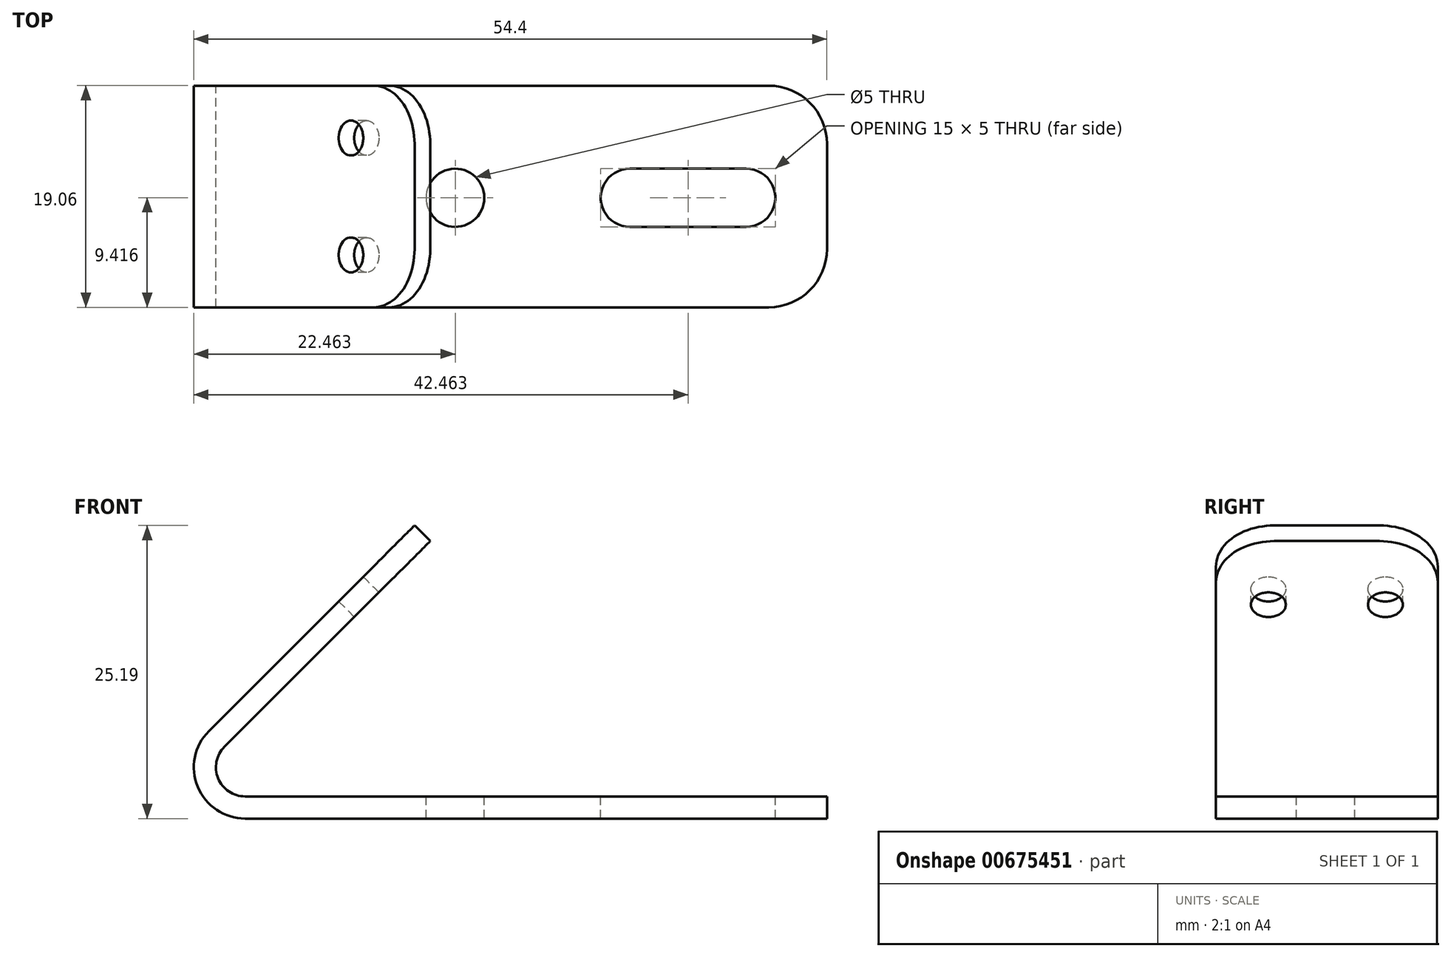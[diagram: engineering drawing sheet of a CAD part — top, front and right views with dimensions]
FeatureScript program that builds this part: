
annotation { "Feature Type Name" : "Feature", "Feature Type Description" : "" }
export const myFeature = defineFeature(function(context is Context, id is Id, definition is map)
    precondition{}
    {
        {
            var Q0;
            Q0=qCreatedBy(makeId("Front.planeOp"),FACE);
            var sketch = newSketch(context, id + "F0", { "sketchPlane" : qUnion([Q0])});
            skLineSegment(sketch, "E0", {"start": v(-36.54, -1.9) * mm, "end": v(13.46, -1.9) * mm});
            skLineSegment(sketch, "E1", {"start": v(13.46, 0) * mm, "end": v(-47.16, 0) * mm});
            skLineSegment(sketch, "E2", {"start": v(-39.65, 5.6) * mm, "end": v(-21.97, 23.28) * mm});
            skPoint(sketch, "E3.visualSharp", {"position": v(-47.16, -1.9) * mm});
            skArc(sketch, "E3.filletArc", {"start": v(-39.65, 5.6) * mm, "mid": v(-40.6, 0.8) * mm, "end": v(-36.54, -1.9) * mm});
            skLineSegment(sketch, "E4", {"start": v(-21.97, 23.28) * mm, "end": v(-20.63, 21.94) * mm});
            skLineSegment(sketch, "E5", {"start": v(-20.63, 21.94) * mm, "end": v(-38.3, 4.26) * mm});
            skArc(sketch, "E6", {"start": v(-38.3, 4.26) * mm, "mid": v(-38.85, 1.54) * mm, "end": v(-36.54, 0) * mm});
            skLineSegment(sketch, "E7", {"start": v(13.46, 0) * mm, "end": v(13.46, -1.9) * mm});
            skSolve(sketch);
        }
        {
            var Q0;
            Q0=qCreatedBy(makeId("Top.planeOp"),FACE);
            var sketch = newSketch(context, id + "F1", { "sketchPlane" : qUnion([Q0])});
            skLineSegment(sketch, "E8.0", {"start": v(13.52, -9.64) * mm, "end": v(13.52, 9.41) * mm});
            skLineSegment(sketch, "E9.0", {"start": v(13.52, 9.41) * mm, "end": v(-36.48, 9.41) * mm});
            skLineSegment(sketch, "E10.0", {"start": v(13.52, -9.64) * mm, "end": v(-36.48, -9.64) * mm});
            skLineSegment(sketch, "E11", {"start": v(13.52, -0.11) * mm, "end": v(9.02, -0.11) * mm});
            skLineSegment(sketch, "E12", {"start": v(9.02, -0.11) * mm, "end": v(-5.98, -0.11) * mm});
            skLineSegment(sketch, "E13", {"start": v(9.02, -0.11) * mm, "end": v(9.02, 2.39) * mm});
            skCircle(sketch, "E14", {"center": v(6.52, -0.11) * mm, "radius": 2.5 * mm});
            skCircle(sketch, "E15", {"center": v(-3.48, -0.11) * mm, "radius": 2.5 * mm});
            skLineSegment(sketch, "E16", {"start": v(-3.48, 2.39) * mm, "end": v(6.52, 2.39) * mm});
            skLineSegment(sketch, "E17", {"start": v(-3.48, -2.61) * mm, "end": v(6.52, -2.61) * mm});
            skCircle(sketch, "E18", {"center": v(-18.48, -0.11) * mm, "radius": 2.5 * mm});
            skSolve(sketch);
        }
        {
            var Q0;
            Q0=qSketchRegion(id+"F0",true);
            extrude(context, id + "F2", {"entities" : qUnion([Q0]), "endBound" : BoundingType.SYMMETRIC, "depth" : 19.05 * mm, "offsetDistance" : 25.4 * mm});
        }
        {
            var Q0;
            Q0=qSketchRegion(id+"F1",true);
            extrude(context, id + "F3", {"entities" : qUnion([Q0]), "operationType" : NewBodyOperationType.REMOVE, "endBound" : BoundingType.THROUGH_ALL, "oppositeDirection" : true, "depth" : 25.4 * mm, "offsetDistance" : 25.4 * mm});
        }
        {
            var Q0;
            Q0=makeQuery(id+"F2.opExtrude","SWEPT_FACE",FACE,{"disambiguationData":[OSD([sQuery(id+"F0.wireOp",EDGE,"E2")])]});
            var sketch = newSketch(context, id + "F4", { "sketchPlane" : qUnion([Q0])});
            skLineSegment(sketch, "E19.0", {"start": v(9.52, 0.7) * mm, "end": v(-9.52, 0.7) * mm});
            skLineSegment(sketch, "E19.1", {"start": v(9.52, -24.3) * mm, "end": v(-9.52, -24.3) * mm});
            skLineSegment(sketch, "E19.2", {"start": v(-9.53, -24.3) * mm, "end": v(-9.53, 0.7) * mm});
            skLineSegment(sketch, "E19.3", {"start": v(9.52, -24.3) * mm, "end": v(9.52, 0.7) * mm});
            skLineSegment(sketch, "E20", {"start": v(-9.53, 0.7) * mm, "end": v(-9.53, -6.8) * mm});
            skCircle(sketch, "E21", {"center": v(-5.03, -6.8) * mm, "radius": 1.5 * mm});
            skLineSegment(sketch, "E22", {"start": v(9.52, -28.7) * mm, "end": v(-9.53, -28.7) * mm});
            skCircle(sketch, "E23", {"center": v(5.02, -6.8) * mm, "radius": 1.5 * mm});
            skSolve(sketch);
        }
        {
            var Q0;
            Q0=makeQuery(id+"F4.imprint","IMPRINT",FACE,{"disambiguationData":[TD([[makeQuery(id+"F4.imprint","IMPRINT",EDGE,{"derivedFrom":sQuery(id+"F4.wireOp",EDGE,"E21")}),1.0]])]});
            var Q1;
            Q1=makeQuery(id+"F4.imprint","IMPRINT",FACE,{"disambiguationData":[TD([[makeQuery(id+"F4.imprint","IMPRINT",EDGE,{"derivedFrom":sQuery(id+"F4.wireOp",EDGE,"E23")}),1.0]])]});
            extrude(context, id + "F5", {"entities" : qUnion([Q0, Q1]), "operationType" : NewBodyOperationType.REMOVE, "endBound" : BoundingType.UP_TO_NEXT, "oppositeDirection" : true, "depth" : 25.4 * mm, "offsetDistance" : 25.4 * mm});
        }
        {
            var Q0;
            Q0=makeQuery(id+"F2.opExtrude","CAP_EDGE",EDGE,{"disambiguationData":[OSD([sQuery(id+"F0.wireOp",EDGE,"E4")])],"isStart":true});
            var Q1;
            Q1=makeQuery(id+"F2.opExtrude","CAP_EDGE",EDGE,{"disambiguationData":[OSD([sQuery(id+"F0.wireOp",EDGE,"E7")])],"isStart":true});
            var Q2;
            Q2=makeQuery(id+"F2.opExtrude","CAP_EDGE",EDGE,{"disambiguationData":[OSD([sQuery(id+"F0.wireOp",EDGE,"E7")])],"isStart":false});
            var Q3;
            Q3=makeQuery(id+"F2.opExtrude","CAP_EDGE",EDGE,{"disambiguationData":[OSD([sQuery(id+"F0.wireOp",EDGE,"E4")])],"isStart":false});
            fillet(context, id + "F6", {"entities" : qUnion([Q0, Q1, Q2, Q3]), "radius" : 5 * mm, "tangentPropagation" : true, "allowEdgeOverflow" : false});
        }
    });
